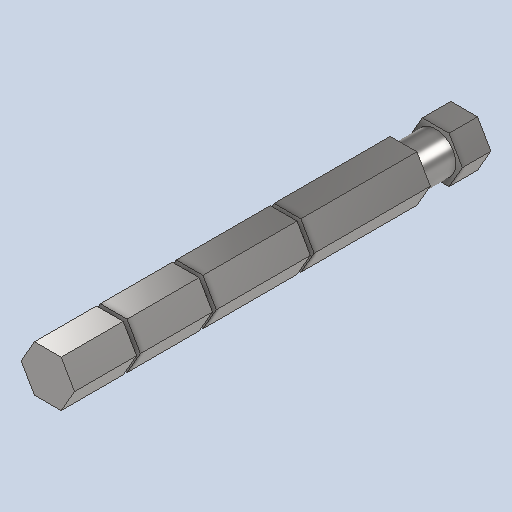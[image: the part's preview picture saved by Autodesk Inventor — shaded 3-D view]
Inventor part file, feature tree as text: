
AUTODESK INVENTOR PART (.ipt)
format: ipt  version: 2025.1 (Build 291241020, 241B)  size: 258,560 bytes
history: native  units: in
note: dims shown in document units (in); Inventor stores cm internally (conversion verified against a paired STEP export)
features: sketch x7, extrude x5, plane x4, other x1, hole x1, projected_geometry x1
ambient origin geometry x8: Origin, YZ Plane, XZ Plane, XY Plane, X Axis, Y Axis, Z Axis, Center Point
bodies: Solid1 (feature_tree)
feature tree (19):
  extrude  "Extrusion1"  Depth=4.5in TaperAngle=0.0deg
  other  "Work Axis1"
  hole  "Hole3"  [1 undecoded]
  plane  "Work Plane4"
  plane  "Work Plane5"
  plane  "Work Plane6"
  plane  "Work Plane7"
  sketch  "Sketch16"  dims[d60=0.392in d62=0.0in d63=0.042in d64=0.4375in]
  extrude  "Extrusion10"  [1 undecoded]
  sketch  "Sketch1"  dims[d0=0.5in d1=4.5in d2=0.0in]
  sketch  "Sketch10"  dims[d33=0.156in d34=0.5in d35=0.375in d36=0.25in d37=0.5635in d38=0.536in d39=0.8108in d40=-0.4in]
  sketch  "Sketch17"  dims[d65=0.092in d66=0.255in d67=0.0in d68=0.0in d69=0.392in d71=0.0in d72=0.042in]
  projected_geometry  "Projected Loop1"
  sketch  "Sketch13"  dims[d45=-1.91in d50=-2.968in]
  sketch  "Sketch15"  dims[d51=0.392in d53=0.0in d54=0.042in d55=-0.67in]
  sketch  "Sketch18"
  extrude  "Extrusion7"  [1 undecoded]
  extrude  "Extrusion9"  Depth=0.042in
  extrude  "Extrusion11"  Depth=0.042in TaperAngle=0.0deg
note: 3 required parameter values undecoded (feature->parameter linkage not recoverable at this tier; creation-order binding heuristic only, values carry confidence <= 0.55)
